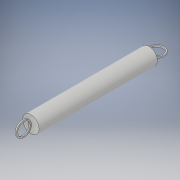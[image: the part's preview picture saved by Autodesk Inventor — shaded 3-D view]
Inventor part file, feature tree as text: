
AUTODESK INVENTOR PART (.ipt)
format: ipt  version: 2018 (Build 220112000, 112)  size: 117,760 bytes
history: native  units: in
note: dims shown in document units (in); Inventor stores cm internally (conversion verified against a paired STEP export)
features: extrude x3, sketch x3
ambient origin geometry x8: Origin, YZ Plane, XZ Plane, XY Plane, X Axis, Y Axis, Z Axis, Center Point
bodies: Solid1 (feature_tree)
feature tree (6):
  extrude  "Extrusion1"  Depth=3.585in TaperAngle=0.0deg
  extrude  "Extrusion2"  Depth=0.2288in
  extrude  "Extrusion3"  Depth=0.04in TaperAngle=0.0deg
  sketch  "Sketch2"  dims[d0=0.5in d1=3.585in d2=0.0in]
  sketch  "Sketch3"  dims[d3=0.2288in d4=0.4575in]
  sketch  "Sketch4"  dims[d5=0.04in d6=0.04in d7=0.0in d8=0.2288in d9=0.4575in d10=0.04in d11=0.04in d12=0.0in]
